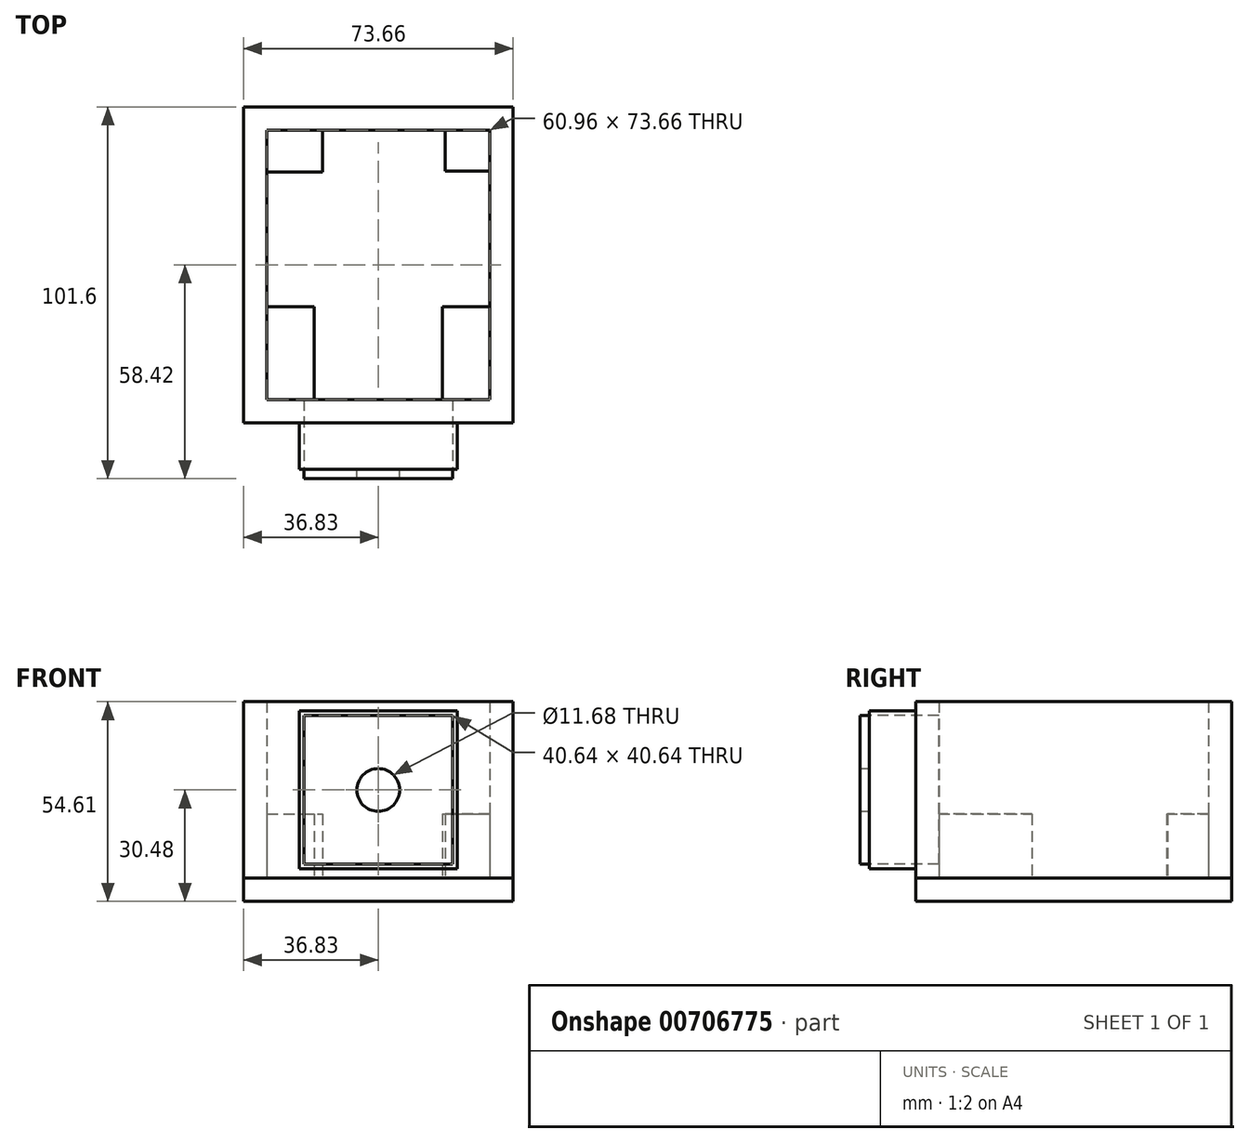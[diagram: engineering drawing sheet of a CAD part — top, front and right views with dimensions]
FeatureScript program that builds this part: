
annotation { "Feature Type Name" : "Feature", "Feature Type Description" : "" }
export const myFeature = defineFeature(function(context is Context, id is Id, definition is map)
    precondition{}
    {
        {
            var Q0;
            Q0=qCreatedBy(makeId("Top.planeOp"),FACE);
            var sketch = newSketch(context, id + "F0", { "sketchPlane" : qUnion([Q0])});
            skLineSegment(sketch, "E0.bottom", {"start": v(0, 0) * mm, "end": v(60.96, 0) * mm});
            skLineSegment(sketch, "E0.top", {"start": v(0, 73.66) * mm, "end": v(60.96, 73.66) * mm});
            skLineSegment(sketch, "E0.left", {"start": v(0, 0) * mm, "end": v(0, 73.66) * mm});
            skLineSegment(sketch, "E0.right", {"start": v(60.96, 0) * mm, "end": v(60.96, 73.66) * mm});
            skLineSegment(sketch, "E1.bottom", {"start": v(-6.35, 80) * mm, "end": v(67.3, 80) * mm});
            skLineSegment(sketch, "E1.top", {"start": v(-6.35, -6.35) * mm, "end": v(67.31, -6.35) * mm});
            skLineSegment(sketch, "E1.left", {"start": v(-6.35, 80) * mm, "end": v(-6.35, -6.35) * mm});
            skLineSegment(sketch, "E1.right", {"start": v(67.3, 80) * mm, "end": v(67.31, -6.35) * mm});
            skLineSegment(sketch, "E2.bottom", {"start": v(0, 25.4) * mm, "end": v(12.95, 25.4) * mm});
            skLineSegment(sketch, "E2.top", {"start": v(0, 0) * mm, "end": v(12.95, 0) * mm});
            skLineSegment(sketch, "E2.left", {"start": v(0, 25.4) * mm, "end": v(0, 0) * mm});
            skLineSegment(sketch, "E2.right", {"start": v(12.95, 25.4) * mm, "end": v(12.95, 0) * mm});
            skLineSegment(sketch, "E3", {"start": v(30.48, 73.66) * mm, "end": v(30.48, 0) * mm, "construction": true});
            skLineSegment(sketch, "E4.MirrorCS", {"start": v(48, 25.4) * mm, "end": v(48, 0) * mm});
            skLineSegment(sketch, "E5.MirrorCS", {"start": v(60.96, 25.4) * mm, "end": v(48, 25.4) * mm});
            skLineSegment(sketch, "E6.bottom", {"start": v(15.24, 73.66) * mm, "end": v(0, 73.66) * mm});
            skLineSegment(sketch, "E6.top", {"start": v(15.24, 62.23) * mm, "end": v(0, 62.23) * mm});
            skLineSegment(sketch, "E6.left", {"start": v(15.24, 73.66) * mm, "end": v(15.24, 62.23) * mm});
            skLineSegment(sketch, "E6.right", {"start": v(0, 73.66) * mm, "end": v(0, 62.23) * mm});
            skLineSegment(sketch, "E7.bottom", {"start": v(48.77, 73.66) * mm, "end": v(60.96, 73.66) * mm});
            skLineSegment(sketch, "E7.top", {"start": v(48.77, 62.48) * mm, "end": v(60.96, 62.48) * mm});
            skLineSegment(sketch, "E7.left", {"start": v(48.77, 73.66) * mm, "end": v(48.77, 62.48) * mm});
            skLineSegment(sketch, "E7.right", {"start": v(60.96, 73.66) * mm, "end": v(60.96, 62.48) * mm});
            skSolve(sketch);
        }
        {
            var Q0;
            {var subQ4=sQuery(id+"F0.wireOp",EDGE,"E6.top");Q0=makeQuery(id+"F0.imprint","IMPRINT",FACE,{"disambiguationData":[TD([[makeQuery(id+"F0.imprint","IMPRINT",EDGE,{"derivedFrom":subQ4}),-1.0]])]});}
            var Q1;
            {var subQ4=sQuery(id+"F0.wireOp",EDGE,"E7.top");Q1=makeQuery(id+"F0.imprint","IMPRINT",FACE,{"disambiguationData":[TD([[makeQuery(id+"F0.imprint","IMPRINT",EDGE,{"derivedFrom":subQ4}),1.0]])]});}
            var Q2;
            {var subQ0=sQuery(id+"F0.wireOp",EDGE,"E4.MirrorCS");Q2=makeQuery(id+"F0.imprint","IMPRINT",FACE,{"disambiguationData":[TD([[makeQuery(id+"F0.imprint","IMPRINT",EDGE,{"derivedFrom":subQ0}),1.0]])]});}
            var Q3;
            {var subQ4=sQuery(id+"F0.wireOp",EDGE,"E2.bottom");Q3=makeQuery(id+"F0.imprint","IMPRINT",FACE,{"disambiguationData":[TD([[makeQuery(id+"F0.imprint","IMPRINT",EDGE,{"derivedFrom":subQ4}),-1.0]])]});}
            extrude(context, id + "F1", {"entities" : qUnion([Q0, Q1, Q2, Q3]), "depth" : 17.53 * mm, "offsetDistance" : 25.4 * mm});
        }
        {
            var Q0;
            Q0=makeQuery(id+"F0.imprint","IMPRINT",FACE,{"disambiguationData":[TD([[makeQuery(id+"F0.imprint","IMPRINT",EDGE,{"derivedFrom":sQuery(id+"F0.wireOp",EDGE,"E1.bottom")}),-1.0]])]});
            extrude(context, id + "F2", {"entities" : qUnion([Q0]), "depth" : 48.26 * mm, "offsetDistance" : 25.4 * mm});
        }
        {
            var Q0;
            {var subQ3=sQuery(id+"F0.wireOp",EDGE,"E2.bottom");Q0=makeQuery(id+"F0.imprint","IMPRINT",FACE,{"disambiguationData":[TD([[makeQuery(id+"F0.imprint","IMPRINT",EDGE,{"derivedFrom":subQ3}),1.0]])]});}
            var Q1;
            {var subQ4=sQuery(id+"F0.wireOp",EDGE,"E2.bottom");Q1=makeQuery(id+"F0.imprint","IMPRINT",FACE,{"disambiguationData":[TD([[makeQuery(id+"F0.imprint","IMPRINT",EDGE,{"derivedFrom":subQ4}),-1.0]])]});}
            var Q2;
            Q2=makeQuery(id+"F0.imprint","IMPRINT",FACE,{"disambiguationData":[TD([[makeQuery(id+"F0.imprint","IMPRINT",EDGE,{"derivedFrom":sQuery(id+"F0.wireOp",EDGE,"E1.bottom")}),-1.0]])]});
            var Q3;
            {var subQ0=sQuery(id+"F0.wireOp",EDGE,"E4.MirrorCS");Q3=makeQuery(id+"F0.imprint","IMPRINT",FACE,{"disambiguationData":[TD([[makeQuery(id+"F0.imprint","IMPRINT",EDGE,{"derivedFrom":subQ0}),1.0]])]});}
            var Q4;
            {var subQ4=sQuery(id+"F0.wireOp",EDGE,"E7.top");Q4=makeQuery(id+"F0.imprint","IMPRINT",FACE,{"disambiguationData":[TD([[makeQuery(id+"F0.imprint","IMPRINT",EDGE,{"derivedFrom":subQ4}),1.0]])]});}
            var Q5;
            {var subQ4=sQuery(id+"F0.wireOp",EDGE,"E6.top");Q5=makeQuery(id+"F0.imprint","IMPRINT",FACE,{"disambiguationData":[TD([[makeQuery(id+"F0.imprint","IMPRINT",EDGE,{"derivedFrom":subQ4}),-1.0]])]});}
            extrude(context, id + "F3", {"entities" : qUnion([Q0, Q1, Q2, Q3, Q4, Q5]), "depth" : -6.35 * mm, "offsetDistance" : 25.4 * mm});
        }
        {
            var Q0;
            Q0=makeQuery(id+"F2.opExtrude","SWEPT_FACE",FACE,{"disambiguationData":[OSD([sQuery(id+"F0.wireOp",EDGE,"E1.top")])]});
            var sketch = newSketch(context, id + "F4", { "sketchPlane" : qUnion([Q0])});
            skLineSegment(sketch, "E8", {"start": v(-6.35, 24.13) * mm, "end": v(67.31, 24.13) * mm, "construction": true});
            skLineSegment(sketch, "E9", {"start": v(30.48, 48.26) * mm, "end": v(30.48, 0) * mm, "construction": true});
            skLineSegment(sketch, "E10.bottom", {"start": v(10.16, 44.45) * mm, "end": v(50.8, 44.45) * mm});
            skLineSegment(sketch, "E10.top", {"start": v(10.16, 3.8) * mm, "end": v(50.8, 3.8) * mm});
            skLineSegment(sketch, "E10.left", {"start": v(10.16, 44.45) * mm, "end": v(10.16, 3.8) * mm});
            skLineSegment(sketch, "E10.right", {"start": v(50.8, 44.45) * mm, "end": v(50.8, 3.8) * mm});
            skSolve(sketch);
        }
        {
            var Q0;
            Q0 = qSketchRegion(id + "F4", true);
            extrude(context, id + "F5", {"entities" : qUnion([Q0]), "operationType" : NewBodyOperationType.REMOVE, "oppositeDirection" : true, "depth" : 6.38 * mm, "offsetDistance" : 25.4 * mm});
        }
        {
            var Q0;
            Q0=makeQuery(id+"F2.opExtrude","SWEPT_FACE",FACE,{"disambiguationData":[OSD([sQuery(id+"F0.wireOp",EDGE,"E1.top")])]});
            var sketch = newSketch(context, id + "F6", { "sketchPlane" : qUnion([Q0])});
            skLineSegment(sketch, "E11.bottom", {"start": v(8.9, 45.72) * mm, "end": v(52.07, 45.72) * mm});
            skLineSegment(sketch, "E11.top", {"start": v(8.9, 2.54) * mm, "end": v(52.07, 2.54) * mm});
            skLineSegment(sketch, "E11.left", {"start": v(8.9, 45.72) * mm, "end": v(8.9, 2.54) * mm});
            skLineSegment(sketch, "E11.right", {"start": v(52.07, 45.72) * mm, "end": v(52.07, 2.54) * mm});
            skSolve(sketch);
        }
        {
            var Q0;
            Q0=makeQuery(id+"F6.imprint","IMPRINT",FACE,{"disambiguationData":[TD([[makeQuery(id+"F6.imprint","IMPRINT",EDGE,{"derivedFrom":sQuery(id+"F6.wireOp",EDGE,"E11.bottom")}),-1.0]])]});
            extrude(context, id + "F7", {"entities" : qUnion([Q0]), "operationType" : NewBodyOperationType.ADD, "depth" : 12.7 * mm, "offsetDistance" : 25.4 * mm});
        }
        {
            var Q0;
            Q0=makeQuery(id+"F7.opExtrude","CAP_FACE",FACE,{"disambiguationData":[OSD([sQuery(id+"F4.wireOp",EDGE,"E10.bottom"),sQuery(id+"F4.wireOp",EDGE,"E10.top"),sQuery(id+"F4.wireOp",EDGE,"E10.left"),sQuery(id+"F4.wireOp",EDGE,"E10.right"),sQuery(id+"F6.wireOp",EDGE,"E11.bottom"),sQuery(id+"F6.wireOp",EDGE,"E11.top"),sQuery(id+"F6.wireOp",EDGE,"E11.left"),sQuery(id+"F6.wireOp",EDGE,"E11.right")])],"isStart":false});
            var sketch = newSketch(context, id + "F8", { "sketchPlane" : qUnion([Q0])});
            skLineSegment(sketch, "E12.bottom", {"start": v(8.9, 45.72) * mm, "end": v(52.07, 45.72) * mm});
            skLineSegment(sketch, "E12.top", {"start": v(8.9, 2.54) * mm, "end": v(52.07, 2.54) * mm});
            skLineSegment(sketch, "E12.left", {"start": v(8.9, 45.72) * mm, "end": v(8.9, 2.54) * mm});
            skLineSegment(sketch, "E12.right", {"start": v(52.07, 45.72) * mm, "end": v(52.07, 2.54) * mm});
            skLineSegment(sketch, "E13", {"start": v(30.48, 45.72) * mm, "end": v(30.48, 3.8) * mm, "construction": true});
            skLineSegment(sketch, "E14", {"start": v(50.8, 24.13) * mm, "end": v(10.16, 24.13) * mm, "construction": true});
            skCircle(sketch, "E15", {"center": v(30.48, 24.13) * mm, "radius": 5.84 * mm});
            skSolve(sketch);
        }
        {
            var Q0;
            Q0=makeQuery(id+"F8.imprint","IMPRINT",FACE,{"disambiguationData":[TD([[makeQuery(id+"F8.imprint","IMPRINT",EDGE,{"derivedFrom":sQuery(id+"F8.wireOp",EDGE,"E15")}),-1.0]])]});
            extrude(context, id + "F9", {"entities" : qUnion([Q0]), "depth" : 2.54 * mm, "offsetDistance" : 25.4 * mm});
        }
    });
